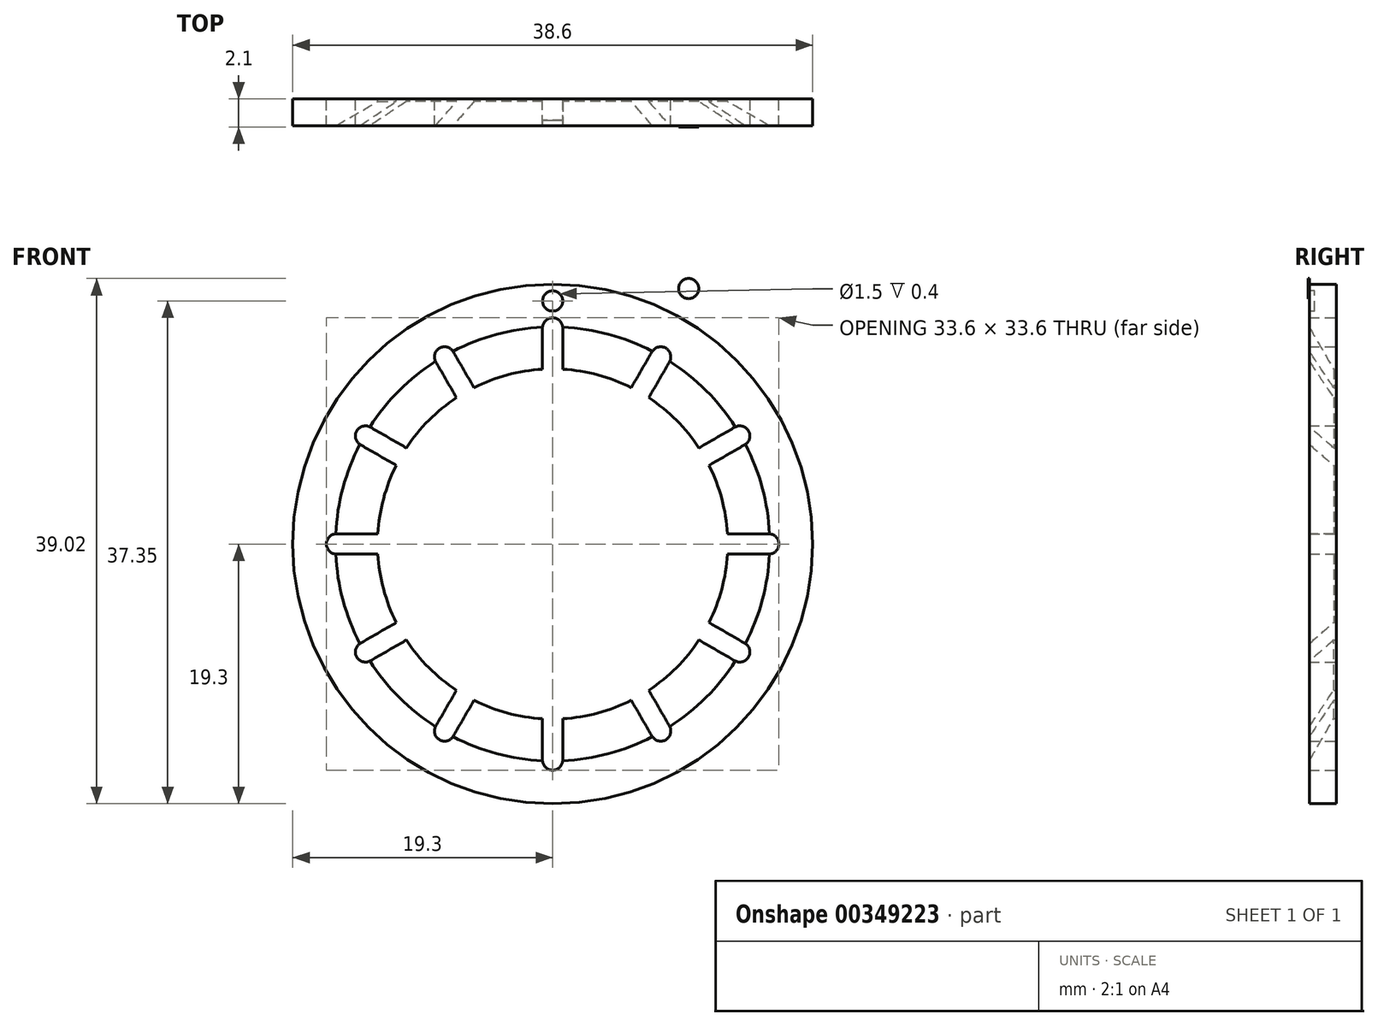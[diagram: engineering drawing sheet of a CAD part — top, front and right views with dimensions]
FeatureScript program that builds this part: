
annotation { "Feature Type Name" : "Feature", "Feature Type Description" : "" }
export const myFeature = defineFeature(function(context is Context, id is Id, definition is map)
    precondition{}
    {
        {
            var Q0;
            Q0=qCreatedBy(makeId("Front.planeOp"),FACE);
            var sketch = newSketch(context, id + "F0", { "sketchPlane" : qUnion([Q0])});
            skCircle(sketch, "E0", {"center": v(0, 0) * mm, "radius": 19.3 * mm});
            skCircle(sketch, "E1", {"center": v(-16.05, 0) * mm, "radius": 0.75 * mm});
            skLineSegment(sketch, "E2", {"start": v(-11.98, 0.75) * mm, "end": v(-11.98, -0.75) * mm});
            skLineSegment(sketch, "E3", {"start": v(-11.98, 0.75) * mm, "end": v(-16.05, 0.75) * mm});
            skLineSegment(sketch, "E4", {"start": v(-11.98, -0.75) * mm, "end": v(-16.05, -0.75) * mm});
            skCircle(sketch, "E5", {"center": v(0, 0) * mm, "radius": 13 * mm});
            skCircle(sketch, "E6.1.0", {"center": v(-13.9, -8.02) * mm, "radius": 0.75 * mm});
            skLineSegment(sketch, "E6.1.1", {"start": v(-10, -6.64) * mm, "end": v(-13.52, -8.67) * mm});
            skLineSegment(sketch, "E6.1.2", {"start": v(-10.75, -5.34) * mm, "end": v(-14.27, -7.38) * mm});
            skCircle(sketch, "E6.2.0", {"center": v(-8.03, -13.9) * mm, "radius": 0.75 * mm});
            skLineSegment(sketch, "E6.2.1", {"start": v(-5.34, -10.75) * mm, "end": v(-7.38, -14.27) * mm});
            skLineSegment(sketch, "E6.2.2", {"start": v(-6.64, -10) * mm, "end": v(-8.67, -13.52) * mm});
            skCircle(sketch, "E6.3.0", {"center": v(0, -16.05) * mm, "radius": 0.75 * mm});
            skLineSegment(sketch, "E6.3.1", {"start": v(0.75, -11.98) * mm, "end": v(0.75, -16.05) * mm});
            skLineSegment(sketch, "E6.3.2", {"start": v(-0.75, -11.98) * mm, "end": v(-0.75, -16.05) * mm});
            skCircle(sketch, "E6.4.0", {"center": v(8.02, -13.9) * mm, "radius": 0.75 * mm});
            skLineSegment(sketch, "E6.4.1", {"start": v(6.64, -10) * mm, "end": v(8.67, -13.52) * mm});
            skLineSegment(sketch, "E6.4.2", {"start": v(5.34, -10.75) * mm, "end": v(7.38, -14.27) * mm});
            skCircle(sketch, "E6.5.0", {"center": v(13.9, -8.02) * mm, "radius": 0.75 * mm});
            skLineSegment(sketch, "E6.5.1", {"start": v(10.75, -5.34) * mm, "end": v(14.27, -7.38) * mm});
            skLineSegment(sketch, "E6.5.2", {"start": v(10, -6.64) * mm, "end": v(13.52, -8.67) * mm});
            skCircle(sketch, "E6.6.0", {"center": v(16.05, 0) * mm, "radius": 0.75 * mm});
            skLineSegment(sketch, "E6.6.1", {"start": v(11.98, 0.75) * mm, "end": v(16.05, 0.75) * mm});
            skLineSegment(sketch, "E6.6.2", {"start": v(11.98, -0.75) * mm, "end": v(16.05, -0.75) * mm});
            skCircle(sketch, "E6.7.0", {"center": v(13.9, 8.02) * mm, "radius": 0.75 * mm});
            skLineSegment(sketch, "E6.7.1", {"start": v(10, 6.64) * mm, "end": v(13.52, 8.67) * mm});
            skLineSegment(sketch, "E6.7.2", {"start": v(10.75, 5.34) * mm, "end": v(14.27, 7.38) * mm});
            skCircle(sketch, "E6.8.0", {"center": v(8.03, 13.9) * mm, "radius": 0.75 * mm});
            skLineSegment(sketch, "E6.8.1", {"start": v(5.34, 10.75) * mm, "end": v(7.38, 14.27) * mm});
            skLineSegment(sketch, "E6.8.2", {"start": v(6.64, 10) * mm, "end": v(8.67, 13.52) * mm});
            skCircle(sketch, "E6.9.0", {"center": v(0, 16.05) * mm, "radius": 0.75 * mm});
            skLineSegment(sketch, "E6.9.1", {"start": v(-0.75, 11.98) * mm, "end": v(-0.75, 16.05) * mm});
            skLineSegment(sketch, "E6.9.2", {"start": v(0.75, 11.98) * mm, "end": v(0.75, 16.05) * mm});
            skCircle(sketch, "E6.10.0", {"center": v(-8.03, 13.9) * mm, "radius": 0.75 * mm});
            skLineSegment(sketch, "E6.10.1", {"start": v(-6.64, 10) * mm, "end": v(-8.67, 13.52) * mm});
            skLineSegment(sketch, "E6.10.2", {"start": v(-5.34, 10.75) * mm, "end": v(-7.38, 14.27) * mm});
            skCircle(sketch, "E6.11.0", {"center": v(-13.9, 8.03) * mm, "radius": 0.75 * mm});
            skLineSegment(sketch, "E6.11.1", {"start": v(-10.75, 5.34) * mm, "end": v(-14.27, 7.38) * mm});
            skLineSegment(sketch, "E6.11.2", {"start": v(-10, 6.64) * mm, "end": v(-13.52, 8.67) * mm});
            skSolve(sketch);
        }
        {
            var Q0;
            Q0=makeQuery(id+"F0.imprint","IMPRINT",FACE,{"disambiguationData":[TD([[makeQuery(id+"F0.imprint","IMPRINT",EDGE,{"derivedFrom":sQuery(id+"F0.wireOp",EDGE,"E0")}),1.0]])]});
            extrude(context, id + "F1", {"entities" : qUnion([Q0]), "depth" : 2 * mm});
        }
        {
            var Q0;
            {var subQ0=sQuery(id+"F0.wireOp",EDGE,"E5");Q0=makeQuery(id+"F1.opExtrude","CAP_EDGE",EDGE,{"disambiguationData":[OSD([subQ0]),TDD([makeQuery(id+"F0.imprint","IMPRINT",EDGE,{"disambiguationData":[TD([[makeQuery(id+"F0.imprint","INTERSECT",VERTEX,{"derivedFrom":[subQ0,sQuery(id+"F0.wireOp",EDGE,"E6.10.1")]}),-1.0]])],"derivedFrom":subQ0})])],"isStart":false});}
            var Q1;
            {var subQ0=sQuery(id+"F0.wireOp",EDGE,"E5");Q1=makeQuery(id+"F1.opExtrude","CAP_EDGE",EDGE,{"disambiguationData":[OSD([subQ0]),TDD([makeQuery(id+"F0.imprint","IMPRINT",EDGE,{"disambiguationData":[TD([[makeQuery(id+"F0.imprint","INTERSECT",VERTEX,{"derivedFrom":[subQ0,sQuery(id+"F0.wireOp",EDGE,"E6.9.1")]}),-1.0]])],"derivedFrom":subQ0})])],"isStart":false});}
            var Q2;
            {var subQ0=sQuery(id+"F0.wireOp",EDGE,"E5");Q2=makeQuery(id+"F1.opExtrude","CAP_EDGE",EDGE,{"disambiguationData":[OSD([subQ0]),TDD([makeQuery(id+"F0.imprint","IMPRINT",EDGE,{"disambiguationData":[TD([[makeQuery(id+"F0.imprint","INTERSECT",VERTEX,{"derivedFrom":[subQ0,sQuery(id+"F0.wireOp",EDGE,"E6.8.1")]}),-1.0]])],"derivedFrom":subQ0})])],"isStart":false});}
            var Q3;
            {var subQ0=sQuery(id+"F0.wireOp",EDGE,"E5");Q3=makeQuery(id+"F1.opExtrude","CAP_EDGE",EDGE,{"disambiguationData":[OSD([subQ0]),TDD([makeQuery(id+"F0.imprint","IMPRINT",EDGE,{"disambiguationData":[TD([[makeQuery(id+"F0.imprint","INTERSECT",VERTEX,{"derivedFrom":[subQ0,sQuery(id+"F0.wireOp",EDGE,"E6.7.1")]}),-1.0]])],"derivedFrom":subQ0})])],"isStart":false});}
            var Q4;
            {var subQ0=sQuery(id+"F0.wireOp",EDGE,"E5");Q4=makeQuery(id+"F1.opExtrude","CAP_EDGE",EDGE,{"disambiguationData":[OSD([subQ0]),TDD([makeQuery(id+"F0.imprint","IMPRINT",EDGE,{"disambiguationData":[TD([[makeQuery(id+"F0.imprint","INTERSECT",VERTEX,{"derivedFrom":[subQ0,sQuery(id+"F0.wireOp",EDGE,"E6.7.2")]}),1.0]])],"derivedFrom":subQ0})])],"isStart":false});}
            var Q5;
            {var subQ0=sQuery(id+"F0.wireOp",EDGE,"E5");Q5=makeQuery(id+"F1.opExtrude","CAP_EDGE",EDGE,{"disambiguationData":[OSD([subQ0]),TDD([makeQuery(id+"F0.imprint","IMPRINT",EDGE,{"disambiguationData":[TD([[makeQuery(id+"F0.imprint","INTERSECT",VERTEX,{"derivedFrom":[subQ0,sQuery(id+"F0.wireOp",EDGE,"E6.11.1")]}),-1.0]])],"derivedFrom":subQ0})])],"isStart":false});}
            var Q6;
            {var subQ0=sQuery(id+"F0.wireOp",EDGE,"E5");Q6=makeQuery(id+"F1.opExtrude","CAP_EDGE",EDGE,{"disambiguationData":[OSD([subQ0]),TDD([makeQuery(id+"F0.imprint","IMPRINT",EDGE,{"disambiguationData":[TD([[makeQuery(id+"F0.imprint","INTERSECT",VERTEX,{"derivedFrom":[subQ0,sQuery(id+"F0.wireOp",EDGE,"E6.1.2")]}),1.0]])],"derivedFrom":subQ0})])],"isStart":false});}
            var Q7;
            {var subQ0=sQuery(id+"F0.wireOp",EDGE,"E5");Q7=makeQuery(id+"F1.opExtrude","CAP_EDGE",EDGE,{"disambiguationData":[OSD([subQ0]),TDD([makeQuery(id+"F0.imprint","IMPRINT",EDGE,{"disambiguationData":[TD([[makeQuery(id+"F0.imprint","INTERSECT",VERTEX,{"derivedFrom":[subQ0,sQuery(id+"F0.wireOp",EDGE,"E6.1.1")]}),-1.0]])],"derivedFrom":subQ0})])],"isStart":false});}
            var Q8;
            {var subQ0=sQuery(id+"F0.wireOp",EDGE,"E5");Q8=makeQuery(id+"F1.opExtrude","CAP_EDGE",EDGE,{"disambiguationData":[OSD([subQ0]),TDD([makeQuery(id+"F0.imprint","IMPRINT",EDGE,{"disambiguationData":[TD([[makeQuery(id+"F0.imprint","INTERSECT",VERTEX,{"derivedFrom":[subQ0,sQuery(id+"F0.wireOp",EDGE,"E6.2.1")]}),-1.0]])],"derivedFrom":subQ0})])],"isStart":false});}
            var Q9;
            {var subQ0=sQuery(id+"F0.wireOp",EDGE,"E5");Q9=makeQuery(id+"F1.opExtrude","CAP_EDGE",EDGE,{"disambiguationData":[OSD([subQ0]),TDD([makeQuery(id+"F0.imprint","IMPRINT",EDGE,{"disambiguationData":[TD([[makeQuery(id+"F0.imprint","INTERSECT",VERTEX,{"derivedFrom":[subQ0,sQuery(id+"F0.wireOp",EDGE,"E6.3.1")]}),-1.0]])],"derivedFrom":subQ0})])],"isStart":false});}
            var Q10;
            {var subQ0=sQuery(id+"F0.wireOp",EDGE,"E5");Q10=makeQuery(id+"F1.opExtrude","CAP_EDGE",EDGE,{"disambiguationData":[OSD([subQ0]),TDD([makeQuery(id+"F0.imprint","IMPRINT",EDGE,{"disambiguationData":[TD([[makeQuery(id+"F0.imprint","INTERSECT",VERTEX,{"derivedFrom":[subQ0,sQuery(id+"F0.wireOp",EDGE,"E6.4.1")]}),-1.0]])],"derivedFrom":subQ0})])],"isStart":false});}
            var Q11;
            {var subQ0=sQuery(id+"F0.wireOp",EDGE,"E5");Q11=makeQuery(id+"F1.opExtrude","CAP_EDGE",EDGE,{"disambiguationData":[OSD([subQ0]),TDD([makeQuery(id+"F0.imprint","IMPRINT",EDGE,{"disambiguationData":[TD([[makeQuery(id+"F0.imprint","INTERSECT",VERTEX,{"derivedFrom":[subQ0,sQuery(id+"F0.wireOp",EDGE,"E6.5.1")]}),-1.0]])],"derivedFrom":subQ0})])],"isStart":false});}
            chamfer(context, id + "F2", {"entities" : qUnion([Q0, Q1, Q2, Q3, Q4, Q5, Q6, Q7, Q8, Q9, Q10, Q11]), "chamferType" : ChamferType.OFFSET_ANGLE, "width" : 1.8 * mm, "oppositeDirection" : false, "angle" : 60 * degree, "tangentPropagation" : true});
        }
        {
            var Q0;
            Q0=makeQuery(id+"F1.opExtrude","CAP_FACE",FACE,{"disambiguationData":[OSD([sQuery(id+"F0.wireOp",EDGE,"E0"),sQuery(id+"F0.wireOp",EDGE,"Y9NMyN1v-o5d7-lghG-WsKN-6NdFW2ecFu0y"),sQuery(id+"F0.wireOp",EDGE,"E1"),sQuery(id+"F0.wireOp",EDGE,"03c2fd6c-5843-42d8-9a65-f85bf20bf25a.1.0"),sQuery(id+"F0.wireOp",EDGE,"03c2fd6c-5843-42d8-9a65-f85bf20bf25a.2.0"),sQuery(id+"F0.wireOp",EDGE,"03c2fd6c-5843-42d8-9a65-f85bf20bf25a.3.0"),sQuery(id+"F0.wireOp",EDGE,"03c2fd6c-5843-42d8-9a65-f85bf20bf25a.4.0"),sQuery(id+"F0.wireOp",EDGE,"03c2fd6c-5843-42d8-9a65-f85bf20bf25a.5.0"),sQuery(id+"F0.wireOp",EDGE,"03c2fd6c-5843-42d8-9a65-f85bf20bf25a.6.0"),sQuery(id+"F0.wireOp",EDGE,"03c2fd6c-5843-42d8-9a65-f85bf20bf25a.7.0"),sQuery(id+"F0.wireOp",EDGE,"03c2fd6c-5843-42d8-9a65-f85bf20bf25a.8.0"),sQuery(id+"F0.wireOp",EDGE,"03c2fd6c-5843-42d8-9a65-f85bf20bf25a.9.0"),sQuery(id+"F0.wireOp",EDGE,"03c2fd6c-5843-42d8-9a65-f85bf20bf25a.10.0"),sQuery(id+"F0.wireOp",EDGE,"03c2fd6c-5843-42d8-9a65-f85bf20bf25a.11.0"),sQuery(id+"F0.wireOp",EDGE,"BxhnizZ6-vHCs-sQrz-zzto-1asNhBGzYGK4.bottom"),sQuery(id+"F0.wireOp",EDGE,"BxhnizZ6-vHCs-sQrz-zzto-1asNhBGzYGK4.top"),sQuery(id+"F0.wireOp",EDGE,"Fhgj540H-gIxa-72sk-aY0O-2Q50vkd6YfUv"),sQuery(id+"F0.wireOp",EDGE,"3zmmQ6Xj-aSD5-feOO-QPAq-8sOw0EemzUqW"),sQuery(id+"F0.wireOp",EDGE,"44c23adb-f861-4947-8163-55b8a1efebd0.1.0"),sQuery(id+"F0.wireOp",EDGE,"44c23adb-f861-4947-8163-55b8a1efebd0.1.1"),sQuery(id+"F0.wireOp",EDGE,"44c23adb-f861-4947-8163-55b8a1efebd0.1.2"),sQuery(id+"F0.wireOp",EDGE,"44c23adb-f861-4947-8163-55b8a1efebd0.1.3"),sQuery(id+"F0.wireOp",EDGE,"44c23adb-f861-4947-8163-55b8a1efebd0.2.0"),sQuery(id+"F0.wireOp",EDGE,"44c23adb-f861-4947-8163-55b8a1efebd0.2.1"),sQuery(id+"F0.wireOp",EDGE,"44c23adb-f861-4947-8163-55b8a1efebd0.2.2"),sQuery(id+"F0.wireOp",EDGE,"44c23adb-f861-4947-8163-55b8a1efebd0.2.3"),sQuery(id+"F0.wireOp",EDGE,"44c23adb-f861-4947-8163-55b8a1efebd0.3.0"),sQuery(id+"F0.wireOp",EDGE,"44c23adb-f861-4947-8163-55b8a1efebd0.3.1"),sQuery(id+"F0.wireOp",EDGE,"44c23adb-f861-4947-8163-55b8a1efebd0.3.2"),sQuery(id+"F0.wireOp",EDGE,"44c23adb-f861-4947-8163-55b8a1efebd0.3.3"),sQuery(id+"F0.wireOp",EDGE,"fe5df11c-da87-49fc-9612-6cb8a424eeb9.2.4.0"),sQuery(id+"F0.wireOp",EDGE,"fe5df11c-da87-49fc-9612-6cb8a424eeb9.3.4.0"),sQuery(id+"F0.wireOp",EDGE,"fe5df11c-da87-49fc-9612-6cb8a424eeb9.6.4.0"),sQuery(id+"F0.wireOp",EDGE,"fe5df11c-da87-49fc-9612-6cb8a424eeb9.9.4.0"),sQuery(id+"F0.wireOp",EDGE,"fe5df11c-da87-49fc-9612-6cb8a424eeb9.2.5.0"),sQuery(id+"F0.wireOp",EDGE,"fe5df11c-da87-49fc-9612-6cb8a424eeb9.3.5.0"),sQuery(id+"F0.wireOp",EDGE,"fe5df11c-da87-49fc-9612-6cb8a424eeb9.6.5.0"),sQuery(id+"F0.wireOp",EDGE,"fe5df11c-da87-49fc-9612-6cb8a424eeb9.9.5.0"),sQuery(id+"F0.wireOp",EDGE,"fe5df11c-da87-49fc-9612-6cb8a424eeb9.2.6.0"),sQuery(id+"F0.wireOp",EDGE,"fe5df11c-da87-49fc-9612-6cb8a424eeb9.3.6.0"),sQuery(id+"F0.wireOp",EDGE,"fe5df11c-da87-49fc-9612-6cb8a424eeb9.6.6.0"),sQuery(id+"F0.wireOp",EDGE,"fe5df11c-da87-49fc-9612-6cb8a424eeb9.9.6.0"),sQuery(id+"F0.wireOp",EDGE,"fe5df11c-da87-49fc-9612-6cb8a424eeb9.2.7.0"),sQuery(id+"F0.wireOp",EDGE,"fe5df11c-da87-49fc-9612-6cb8a424eeb9.3.7.0"),sQuery(id+"F0.wireOp",EDGE,"fe5df11c-da87-49fc-9612-6cb8a424eeb9.6.7.0"),sQuery(id+"F0.wireOp",EDGE,"fe5df11c-da87-49fc-9612-6cb8a424eeb9.9.7.0"),sQuery(id+"F0.wireOp",EDGE,"fe5df11c-da87-49fc-9612-6cb8a424eeb9.2.8.0"),sQuery(id+"F0.wireOp",EDGE,"fe5df11c-da87-49fc-9612-6cb8a424eeb9.3.8.0"),sQuery(id+"F0.wireOp",EDGE,"fe5df11c-da87-49fc-9612-6cb8a424eeb9.6.8.0"),sQuery(id+"F0.wireOp",EDGE,"fe5df11c-da87-49fc-9612-6cb8a424eeb9.9.8.0"),sQuery(id+"F0.wireOp",EDGE,"fe5df11c-da87-49fc-9612-6cb8a424eeb9.2.9.0"),sQuery(id+"F0.wireOp",EDGE,"fe5df11c-da87-49fc-9612-6cb8a424eeb9.3.9.0"),sQuery(id+"F0.wireOp",EDGE,"fe5df11c-da87-49fc-9612-6cb8a424eeb9.6.9.0"),sQuery(id+"F0.wireOp",EDGE,"fe5df11c-da87-49fc-9612-6cb8a424eeb9.9.9.0"),sQuery(id+"F0.wireOp",EDGE,"fe5df11c-da87-49fc-9612-6cb8a424eeb9.2.10.0"),sQuery(id+"F0.wireOp",EDGE,"fe5df11c-da87-49fc-9612-6cb8a424eeb9.3.10.0"),sQuery(id+"F0.wireOp",EDGE,"fe5df11c-da87-49fc-9612-6cb8a424eeb9.6.10.0"),sQuery(id+"F0.wireOp",EDGE,"fe5df11c-da87-49fc-9612-6cb8a424eeb9.9.10.0"),sQuery(id+"F0.wireOp",EDGE,"fe5df11c-da87-49fc-9612-6cb8a424eeb9.2.11.0"),sQuery(id+"F0.wireOp",EDGE,"fe5df11c-da87-49fc-9612-6cb8a424eeb9.3.11.0"),sQuery(id+"F0.wireOp",EDGE,"fe5df11c-da87-49fc-9612-6cb8a424eeb9.6.11.0"),sQuery(id+"F0.wireOp",EDGE,"fe5df11c-da87-49fc-9612-6cb8a424eeb9.9.11.0")])],"isStart":false});
            var sketch = newSketch(context, id + "F3", { "sketchPlane" : qUnion([Q0])});
            skPoint(sketch, "E7.endSnap0", {"position": v(0, 16.8) * mm});
            skCircle(sketch, "E8", {"center": v(10.1, 18.97) * mm, "radius": 0.75 * mm});
            skLineSegment(sketch, "E9", {"start": v(0, 16.8) * mm, "end": v(0, 19.3) * mm});
            skCircle(sketch, "E10", {"center": v(0, 18.05) * mm, "radius": 0.75 * mm});
            skSolve(sketch);
        }
        {
            var Q0;
            Q0=makeQuery(id+"F3.imprint","IMPRINT",FACE,{"disambiguationData":[TD([[makeQuery(id+"F3.imprint","IMPRINT",EDGE,{"derivedFrom":sQuery(id+"F3.wireOp",EDGE,"HljZrfdy-sTOT-kmeB-H0E4-6OmDUoZPdeeC")}),1.0]])]});
            var Q1;
            {var subQ0=sQuery(id+"F3.wireOp",EDGE,"E10");var subQ1=sQuery(id+"F3.wireOp",EDGE,"E9");var subQ2=makeQuery(id+"F3.imprint","INTERSECT",VERTEX,{"disambiguationData":[OD(0.0)],"derivedFrom":[subQ1,subQ0]});Q1=makeQuery(id+"F3.imprint","IMPRINT",FACE,{"disambiguationData":[TD([[makeQuery(id+"F3.imprint","IMPRINT",EDGE,{"disambiguationData":[TD([[subQ2,-1.0]])],"derivedFrom":subQ1}),1.0]])]});}
            var Q2;
            {var subQ0=sQuery(id+"F3.wireOp",EDGE,"E10");var subQ1=sQuery(id+"F3.wireOp",EDGE,"E9");var subQ2=makeQuery(id+"F3.imprint","INTERSECT",VERTEX,{"disambiguationData":[OD(0.0)],"derivedFrom":[subQ1,subQ0]});Q2=makeQuery(id+"F3.imprint","IMPRINT",FACE,{"disambiguationData":[TD([[makeQuery(id+"F3.imprint","IMPRINT",EDGE,{"disambiguationData":[TD([[subQ2,-1.0]])],"derivedFrom":subQ1}),-1.0]])]});}
            extrude(context, id + "F4", {"entities" : qUnion([Q0, Q1, Q2]), "operationType" : NewBodyOperationType.REMOVE, "oppositeDirection" : true, "depth" : 0.4 * mm});
        }
        {
            var Q0;
            Q0=makeQuery(id+"F3.imprint","IMPRINT",FACE,{"disambiguationData":[TD([[makeQuery(id+"F3.imprint","IMPRINT",EDGE,{"derivedFrom":sQuery(id+"F3.wireOp",EDGE,"E8")}),1.0]])]});
            extrude(context, id + "F5", {"entities" : qUnion([Q0]), "depth" : 0.1 * mm});
        }
    });
